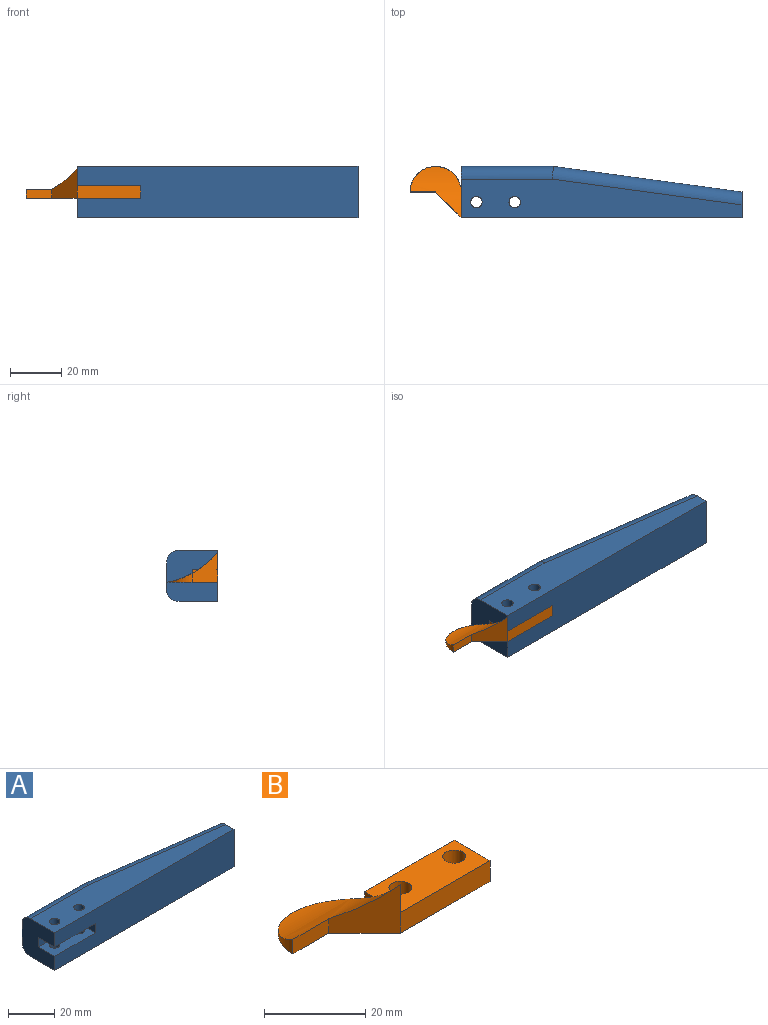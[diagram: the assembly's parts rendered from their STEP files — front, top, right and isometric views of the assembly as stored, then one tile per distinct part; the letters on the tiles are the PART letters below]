
ASSEMBLY  parts=2 mates=1
PART A: 19 faces, bbox 110.7x20x20 mm
  f0: plane 20x20mm, normal (-1,0,0), area 339.3mm2, adj f5,f8,f9,f10,f11,f12,f13,f15
  f1: cylinder r=2.25mm len=7.5mm, axis (0,0,-1), area 106mm2, adj f10,f11
  f2: cylinder r=2.25mm len=7.5mm, axis (0,0,-1), area 106mm2, adj f9,f12
  f3: cylinder r=2.25mm len=7.5mm, axis (0,0,-1), area 106mm2, adj f10,f11
  f4: cylinder r=2.25mm len=7.5mm, axis (0,0,-1), area 106mm2, adj f9,f12
  f5: plane 110x20mm, normal (0,-1,0), area 2075mm2, adj f0,f6,f9,f10,f11,f12,f14
  f6: plane 20x10mm, normal (1,0,0), area 189.2mm2, adj f5,f7,f9,f10,f16,f18
  f7: plane 73.89x10mm, normal (0.13,0.99,0), area 745.6mm2, adj f6,f8,f16,f18
  f8: plane 36.11x10mm, normal (0,1,0), area 361.1mm2, adj f0,f7,f15,f17
  f9: plane 110x15mm, normal (0,0,1), area 1245.4mm2, adj f0,f2,f4,f5,f6,f17,f18
  f10: plane 110x15mm, normal (0,0,-1), area 1245.4mm2, adj f0,f1,f3,f5,f6,f15,f16
  f11: plane 25x10mm, normal (0,0,1), area 218.2mm2, adj f0,f1,f3,f5,f13,f14
  f12: plane 25x10mm, normal (0,0,-1), area 218.2mm2, adj f0,f2,f4,f5,f13,f14
  f13: plane 25x5mm, normal (0,-1,0), area 125mm2, adj f0,f11,f12,f14
  f14: plane 10x5mm, normal (-1,0,0), area 50mm2, adj f5,f11,f12,f13
  f15: cylinder r=5mm len=36.11mm, axis (-1,0,0), area 282.7mm2, adj f0,f8,f10,f16
  f16: cylinder r=5mm len=75.23mm, axis (-0.99,0.13,0), area 586.6mm2, adj f6,f7,f10,f15
  f17: cylinder r=5mm len=36.11mm, axis (1,0,0), area 282.7mm2, adj f0,f8,f9,f18
  f18: cylinder r=5mm len=75.23mm, axis (0.99,-0.13,0), area 586.6mm2, adj f6,f7,f9,f17
PART B: 14 faces, bbox 45x20x11.8 mm
  f0: plane 7.46x6.8mm, normal (1,0,0), area 22.8mm2, adj f2,f10,f12
  f1: cylinder r=10mm len=9.96mm, axis (0,0,-1), area 15.9mm2, adj f6,f11,f12
  f2: plane 11.8x10mm, normal (-0.71,-0.71,0), area 100.1mm2, adj f0,f4,f9,f11,f12
  f3: cylinder r=10mm len=9.96mm, axis (0,0,-1), area 15.9mm2, adj f4,f11,f12
  f4: plane 10x3.48mm, normal (0,-1,0), area 34.8mm2, adj f2,f3,f11,f12
  f5: plane 10x5mm, normal (1,0,0), area 50mm2, adj f6,f9,f10,f11
  f6: plane 25x5mm, normal (0,1,0), area 125mm2, adj f1,f5,f10,f11,f13
  f7: cylinder r=2.25mm len=5mm, axis (0,0,-1), area 70.7mm2, adj f10,f11
  f8: cylinder r=2.25mm len=5mm, axis (0,0,-1), area 70.7mm2, adj f10,f11
  f9: plane 25x5mm, normal (0,-1,0), area 125mm2, adj f2,f5,f10,f11
  f10: plane 25x10mm, normal (0,0,1), area 218.2mm2, adj f0,f5,f6,f7,f8,f9,f13
  f11: plane 45x19.96mm, normal (0,0,-1), area 425.2mm2, adj f1,f2,f3,f4,f5,f6,f7,f8
  f12: cylinder r=33.06mm len=20mm, axis (1,0,0), area 230.2mm2, adj f0,f1,f2,f3,f4,f11,f13
  f13: plane 2.54x1.52mm, normal (-1,0,0), area 2mm2, adj f6,f10,f12
PLACE A t=(9.37,22.33,-17.25)mm
PLACE B t=(39.79,22.33,-9.75)mm
MATE fastened B.f8 <-> A.f3  axis (0,0,1) through (30.37,28.33,-4.75)mm
